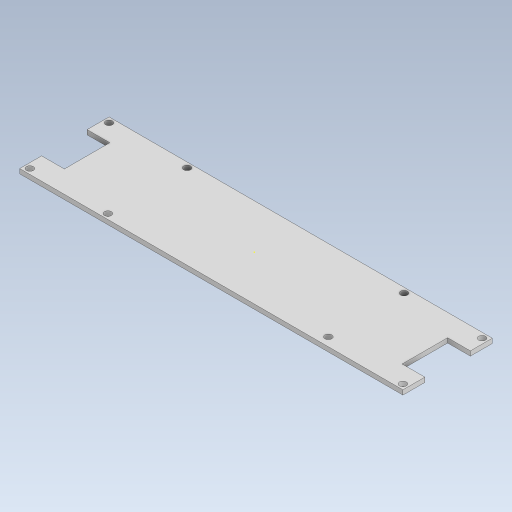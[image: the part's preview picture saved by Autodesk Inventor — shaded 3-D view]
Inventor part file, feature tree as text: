
AUTODESK INVENTOR PART (.ipt)
format: ipt  version: 2023.5 (Build 275446000, 446)  size: 131,072 bytes
history: native  units: in
note: dims shown in document units (in); Inventor stores cm internally (conversion verified against a paired STEP export)
features: extrude x4, sketch x3
ambient origin geometry x8: Origin, YZ Plane, XZ Plane, XY Plane, X Axis, Y Axis, Z Axis, Center Point
bodies: Solid1 (feature_tree)
feature tree (7):
  sketch  "Sketch1"  dims[d0=6.6339in d1=1.5472in]
  extrude  "Extrusion1"  Depth=1.5472in
  extrude  "Extrusion2"  Depth=0.0886in
  extrude  "Extrusion3"  Depth=0.0787in TaperAngle=0.0deg
  sketch  "Sketch3"  dims[d4=0.0886in d5=0.0787in d6=0.0in d7=0.0886in d8=0.0787in d9=0.0in d10=0.7874in d11=0.7874in d12=0.7874in d13=0.7874in d14=0.0787in d15=0.0in d16=0.1181in d17=1.3504in d18=0.1181in d19=0.1181in d20=1.3504in d21=0.1181in d22=0.0787in d23=0.0in]
  extrude  "Extrusion4"  Depth=0.0787in
  sketch  "Sketch2"  dims[d2=0.1181in d3=0.0886in]
